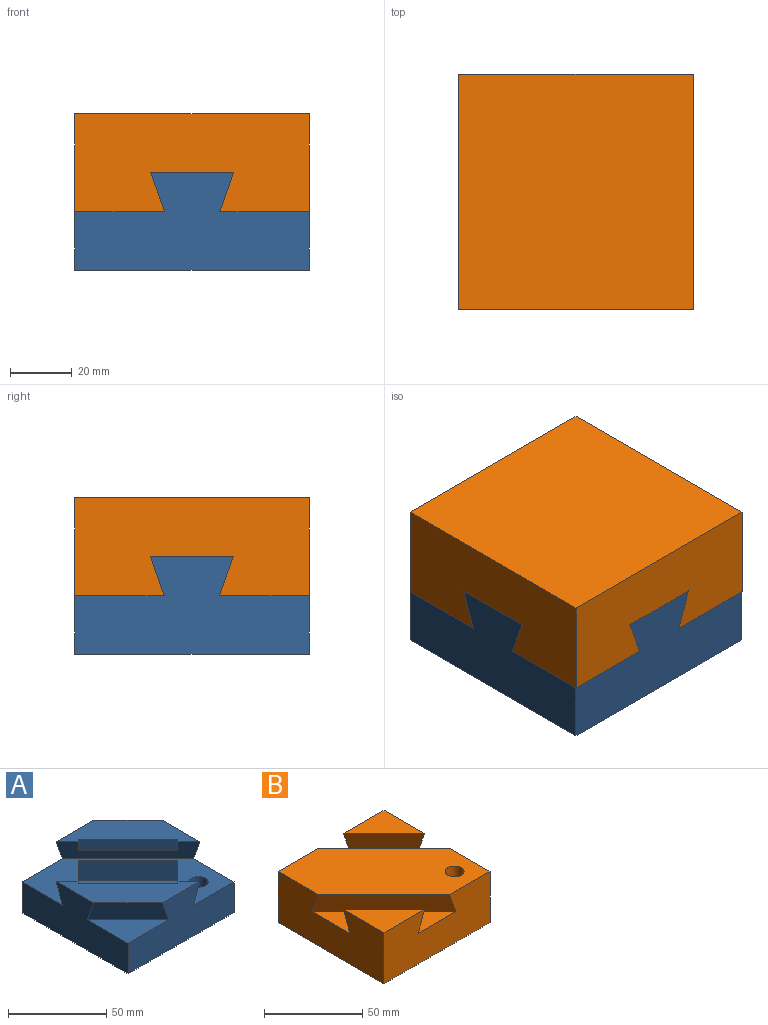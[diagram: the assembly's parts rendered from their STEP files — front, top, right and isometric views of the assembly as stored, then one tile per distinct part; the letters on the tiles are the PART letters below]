
ASSEMBLY  parts=2 mates=1
PART A: 29 faces, bbox 76.2x76.2x31.8 mm
  f0: plane 51.64x51.64mm, normal (0,0,1), area 942.8mm2, adj f2,f3,f9,f13,f22,f23,f24
  f1: plane 51.64x51.64mm, normal (0,0,1), area 942.8mm2, adj f4,f5,f8,f11,f14,f15,f16
  f2: plane 76.2x31.75mm, normal (-1,0,0), area 1736.9mm2, adj f0,f3,f5,f6,f9,f10,f12,f13
  f3: plane 76.2x31.75mm, normal (0,-1,0), area 1736.9mm2, adj f0,f2,f4,f6,f9,f10,f12,f13
  f4: plane 76.2x31.75mm, normal (1,0,0), area 1736.9mm2, adj f1,f3,f5,f6,f7,f8,f10,f11
  f5: plane 76.2x31.75mm, normal (0,1,0), area 1736.9mm2, adj f1,f2,f4,f6,f7,f8,f10,f11
  f6: plane 76.2x76.2mm, normal (0,0,-1), area 5806.4mm2, adj f2,f3,f4,f5
  f7: plane 29.17x29.17mm, normal (0,0,1), area 425.6mm2, adj f4,f5,f8
  f8: plane 29.17x29.17mm, normal (0.69,0.69,-0.24), area 498.6mm2, adj f1,f4,f5,f7
  f9: plane 51.64x51.64mm, normal (0.69,0.69,-0.24), area 561.4mm2, adj f0,f2,f3,f10,f22,f23,f24
  f10: plane 76.2x76.2mm, normal (0,0,1), area 1575.8mm2, adj f2,f3,f4,f5,f9,f11,f18,f19
  f11: plane 51.64x51.64mm, normal (-0.69,-0.69,-0.24), area 561.4mm2, adj f1,f4,f5,f10,f14,f15,f16
  f12: plane 29.17x29.17mm, normal (0,0,1), area 425.6mm2, adj f2,f3,f13
  f13: plane 29.17x29.17mm, normal (-0.69,-0.69,-0.24), area 498.6mm2, adj f0,f2,f3,f12
  f14: plane 35.92x35.92mm, normal (-0.71,-0.71,0), area 342.5mm2, adj f1,f11,f15,f16
  f15: plane 6.74x1.19mm, normal (-0.71,0.71,0), area 5.7mm2, adj f1,f11,f14
  f16: plane 6.74x1.19mm, normal (0.71,-0.71,0), area 5.7mm2, adj f1,f11,f14
  f17: plane 62.86x62.86mm, normal (0,0,1), area 1935.5mm2, adj f18,f19,f20,f21
  f18: plane 35.92x35.92mm, normal (-0.71,-0.71,0), area 645.2mm2, adj f10,f17,f19,f20
  f19: plane 26.94x26.94mm, normal (-0.71,0.71,0), area 483.9mm2, adj f10,f17,f18,f21
  f20: plane 26.94x26.94mm, normal (0.71,-0.71,0), area 483.9mm2, adj f10,f17,f18,f21
  f21: plane 35.92x35.92mm, normal (0.71,0.71,0), area 645.2mm2, adj f10,f17,f19,f20
  f22: plane 35.92x35.92mm, normal (0.71,0.71,0), area 342.5mm2, adj f0,f9,f23,f24
  f23: plane 6.74x1.19mm, normal (0.71,-0.71,0), area 5.7mm2, adj f0,f9,f22
  f24: plane 6.74x1.19mm, normal (-0.71,0.71,0), area 5.7mm2, adj f0,f9,f22
  f25: cylinder r=3.17mm len=6.35mm, axis (0,0,1), area 63.3mm2, adj f26,f28
  f26: plane 9.53x9.53mm, normal (0,0,1), area 39.6mm2, adj f25,f27
  f27: cylinder r=4.76mm len=9.53mm, axis (0,0,1), area 190mm2, adj f10,f26
  f28: cone r=0mm half-angle=59deg, axis (0,0,1), area 36.9mm2, adj f25
PART B: 16 faces, bbox 76.2x76.2x31.8 mm
  f0: plane 76.2x76.2mm, normal (0,0,1), area 3511.3mm2, adj f2,f3,f4,f5,f8,f12,f15
  f1: plane 29.17x29.17mm, normal (0,0,1), area 425.6mm2, adj f2,f3,f11
  f2: plane 76.2x31.75mm, normal (-1,0,0), area 2134.1mm2, adj f0,f1,f3,f5,f7,f11,f12,f13
  f3: plane 76.2x31.75mm, normal (0,-1,0), area 2134.1mm2, adj f0,f1,f2,f4,f7,f11,f12,f13
  f4: plane 76.2x31.75mm, normal (1,0,0), area 2134.1mm2, adj f0,f3,f5,f6,f7,f8,f9,f10
  f5: plane 76.2x31.75mm, normal (0,1,0), area 2134.1mm2, adj f0,f2,f4,f6,f7,f8,f9,f10
  f6: plane 29.17x29.17mm, normal (0,0,1), area 425.6mm2, adj f4,f5,f9
  f7: plane 76.2x76.2mm, normal (0,0,-1), area 5806.4mm2, adj f2,f3,f4,f5
  f8: plane 51.64x51.64mm, normal (0.69,0.69,-0.24), area 914.4mm2, adj f0,f4,f5,f10
  f9: plane 29.17x29.17mm, normal (-0.69,-0.69,-0.24), area 498.6mm2, adj f4,f5,f6,f10
  f10: plane 51.64x51.64mm, normal (0,0,1), area 1028.2mm2, adj f4,f5,f8,f9
  f11: plane 29.17x29.17mm, normal (0.69,0.69,-0.24), area 498.6mm2, adj f1,f2,f3,f13
  f12: plane 51.64x51.64mm, normal (-0.69,-0.69,-0.24), area 914.4mm2, adj f0,f2,f3,f13
  f13: plane 51.64x51.64mm, normal (0,0,1), area 1028.2mm2, adj f2,f3,f11,f12
  f14: cone r=0mm half-angle=59deg, axis (0,0,1), area 83.1mm2, adj f15
  f15: cylinder r=4.76mm len=15.88mm, axis (0,0,1), area 475mm2, adj f0,f14
PLACE A at identity
PLACE B rot(axis=(0.71,-0.71,0),180deg) t=(76.2,76.2,50.8)mm
MATE fastened B.f6 <-> A.f12  axis (0,0,1) through (0,0,19.05)mm
